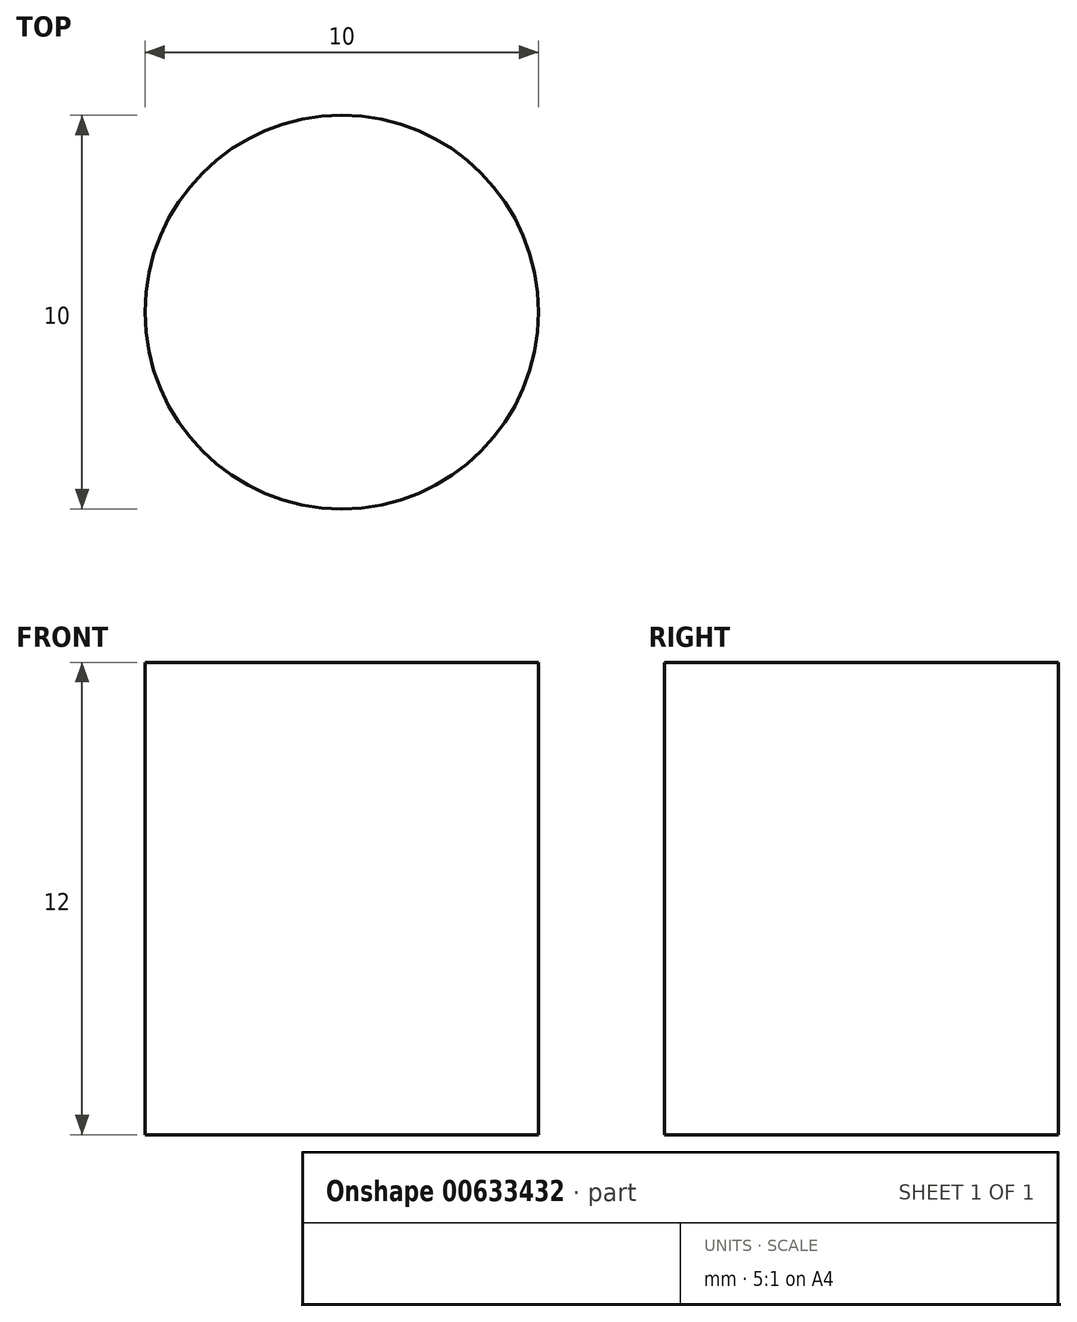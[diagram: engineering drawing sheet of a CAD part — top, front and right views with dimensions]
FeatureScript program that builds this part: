
annotation { "Feature Type Name" : "Feature", "Feature Type Description" : "" }
export const myFeature = defineFeature(function(context is Context, id is Id, definition is map)
    precondition{}
    {
        {
            var Q0;
            Q0=qCreatedBy(makeId("Top.planeOp"),FACE);
            var sketch = newSketch(context, id + "F0", { "sketchPlane" : qUnion([Q0])});
            skCircle(sketch, "E0", {"center": v(0, 0) * mm, "radius": 5 * mm});
            skSolve(sketch);
        }
        {
            var Q0;
            Q0 = qSketchRegion(id + "F0", true);
            extrude(context, id + "F1", {"entities" : qUnion([Q0]), "depth" : 12 * mm, "offsetDistance" : 25 * mm});
        }
    });
